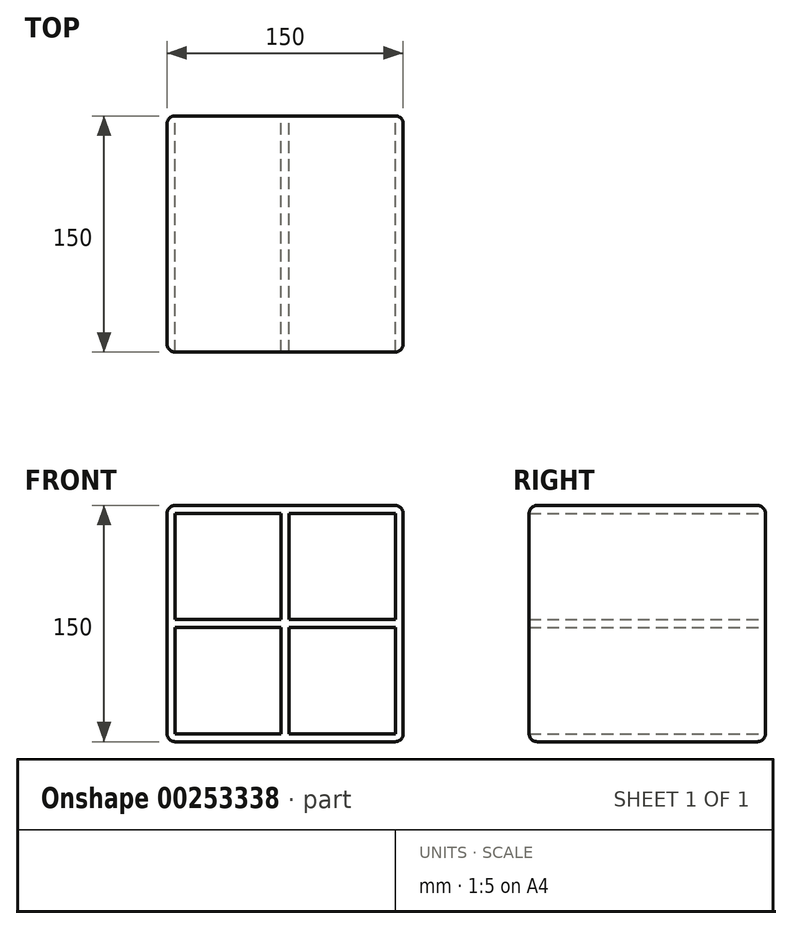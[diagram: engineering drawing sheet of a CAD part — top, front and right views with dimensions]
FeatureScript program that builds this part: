
annotation { "Feature Type Name" : "Feature", "Feature Type Description" : "" }
export const myFeature = defineFeature(function(context is Context, id is Id, definition is map)
    precondition{}
    {
        {
            var Q0;
            Q0=qCreatedBy(makeId("Front.planeOp"),FACE);
            var sketch = newSketch(context, id + "F0", { "sketchPlane" : qUnion([Q0])});
            skLineSegment(sketch, "E0.bottom", {"start": v(0, 0) * mm, "end": v(150, 0) * mm});
            skLineSegment(sketch, "E0.top", {"start": v(0, 150) * mm, "end": v(150, 150) * mm});
            skLineSegment(sketch, "E0.left", {"start": v(0, 0) * mm, "end": v(0, 150) * mm});
            skLineSegment(sketch, "E0.right", {"start": v(150, 0) * mm, "end": v(150, 150) * mm});
            skLineSegment(sketch, "E1.0", {"start": v(5, 145) * mm, "end": v(72.5, 145) * mm});
            skLineSegment(sketch, "E1.1", {"start": v(5, 5) * mm, "end": v(5, 72.5) * mm});
            skLineSegment(sketch, "E1.2", {"start": v(5, 5) * mm, "end": v(72.5, 5) * mm});
            skLineSegment(sketch, "E1.3", {"start": v(145, 5) * mm, "end": v(145, 72.5) * mm});
            skLineSegment(sketch, "E2", {"start": v(72.5, 5) * mm, "end": v(72.5, 72.5) * mm});
            skLineSegment(sketch, "E3.0", {"start": v(77.5, 5) * mm, "end": v(77.5, 72.5) * mm});
            skLineSegment(sketch, "E4", {"start": v(145, 77.5) * mm, "end": v(77.5, 77.5) * mm});
            skLineSegment(sketch, "E5.0", {"start": v(145, 72.5) * mm, "end": v(77.5, 72.5) * mm});
            skLineSegment(sketch, "E6.trimOffspring", {"start": v(72.5, 77.5) * mm, "end": v(5, 77.5) * mm});
            skLineSegment(sketch, "E7.trimOffspring", {"start": v(72.5, 77.5) * mm, "end": v(72.5, 145) * mm});
            skLineSegment(sketch, "E8.trimOffspring", {"start": v(72.5, 72.5) * mm, "end": v(5, 72.5) * mm});
            skLineSegment(sketch, "E9.trimOffspring", {"start": v(77.5, 77.5) * mm, "end": v(77.5, 145) * mm});
            skLineSegment(sketch, "E10.trimOffspring", {"start": v(5, 77.5) * mm, "end": v(5, 145) * mm});
            skLineSegment(sketch, "E11.trimOffspring", {"start": v(77.5, 145) * mm, "end": v(145, 145) * mm});
            skLineSegment(sketch, "E12.trimOffspring", {"start": v(145, 77.5) * mm, "end": v(145, 145) * mm});
            skLineSegment(sketch, "E13.trimOffspring", {"start": v(77.5, 5) * mm, "end": v(145, 5) * mm});
            skSolve(sketch);
        }
        {
            var Q0;
            Q0 = qSketchRegion(id + "F0", true);
            extrude(context, id + "F1", {"entities" : qUnion([Q0]), "depth" : 150 * mm});
        }
        {
            var Q0;
            Q0=makeQuery(id+"F1.opExtrude","SWEPT_EDGE",EDGE,{"disambiguationData":[OSD([sQuery(id+"F0.wireOp",EDGE,"E0.top"),sQuery(id+"F0.wireOp",EDGE,"E0.right")])]});
            fillet(context, id + "F2", {"entities" : qUnion([Q0]), "radius" : 5 * mm, "tangentPropagation" : true, "allowEdgeOverflow" : false});
        }
        {
            var Q0;
            Q0=makeQuery(id+"F1.opExtrude","CAP_EDGE",EDGE,{"disambiguationData":[OSD([sQuery(id+"F0.wireOp",EDGE,"E0.top")])],"isStart":false});
            var Q1;
            Q1=makeQuery(id+"F1.opExtrude","CAP_EDGE",EDGE,{"disambiguationData":[OSD([sQuery(id+"F0.wireOp",EDGE,"E0.right")])],"isStart":false});
            var Q2;
            Q2=makeQuery(id+"F1.opExtrude","CAP_EDGE",EDGE,{"disambiguationData":[OSD([sQuery(id+"F0.wireOp",EDGE,"E0.top")])],"isStart":true});
            var Q3;
            Q3=makeQuery(id+"F1.opExtrude","SWEPT_EDGE",EDGE,{"disambiguationData":[OSD([sQuery(id+"F0.wireOp",EDGE,"E0.top"),sQuery(id+"F0.wireOp",EDGE,"E0.left")])]});
            var Q4;
            Q4=makeQuery(id+"F1.opExtrude","CAP_EDGE",EDGE,{"disambiguationData":[OSD([sQuery(id+"F0.wireOp",EDGE,"E0.bottom")])],"isStart":false});
            var Q5;
            Q5=makeQuery(id+"F1.opExtrude","SWEPT_EDGE",EDGE,{"disambiguationData":[OSD([sQuery(id+"F0.wireOp",EDGE,"E0.bottom"),sQuery(id+"F0.wireOp",EDGE,"E0.right")])]});
            var Q6;
            Q6=makeQuery(id+"F1.opExtrude","CAP_EDGE",EDGE,{"disambiguationData":[OSD([sQuery(id+"F0.wireOp",EDGE,"E0.left")])],"isStart":false});
            var Q7;
            Q7=makeQuery(id+"F1.opExtrude","CAP_EDGE",EDGE,{"disambiguationData":[OSD([sQuery(id+"F0.wireOp",EDGE,"E0.right")])],"isStart":true});
            var Q8;
            Q8=makeQuery(id+"F1.opExtrude","CAP_EDGE",EDGE,{"disambiguationData":[OSD([sQuery(id+"F0.wireOp",EDGE,"E0.left")])],"isStart":true});
            var Q9;
            Q9=makeQuery(id+"F1.opExtrude","SWEPT_EDGE",EDGE,{"disambiguationData":[OSD([sQuery(id+"F0.wireOp",EDGE,"E0.bottom"),sQuery(id+"F0.wireOp",EDGE,"E0.left")])]});
            var Q10;
            Q10=makeQuery(id+"F1.opExtrude","CAP_EDGE",EDGE,{"disambiguationData":[OSD([sQuery(id+"F0.wireOp",EDGE,"E0.bottom")])],"isStart":true});
            fillet(context, id + "F3", {"entities" : qUnion([Q0, Q1, Q2, Q3, Q4, Q5, Q6, Q7, Q8, Q9, Q10]), "radius" : 5 * mm, "tangentPropagation" : true, "allowEdgeOverflow" : false});
        }
    });
